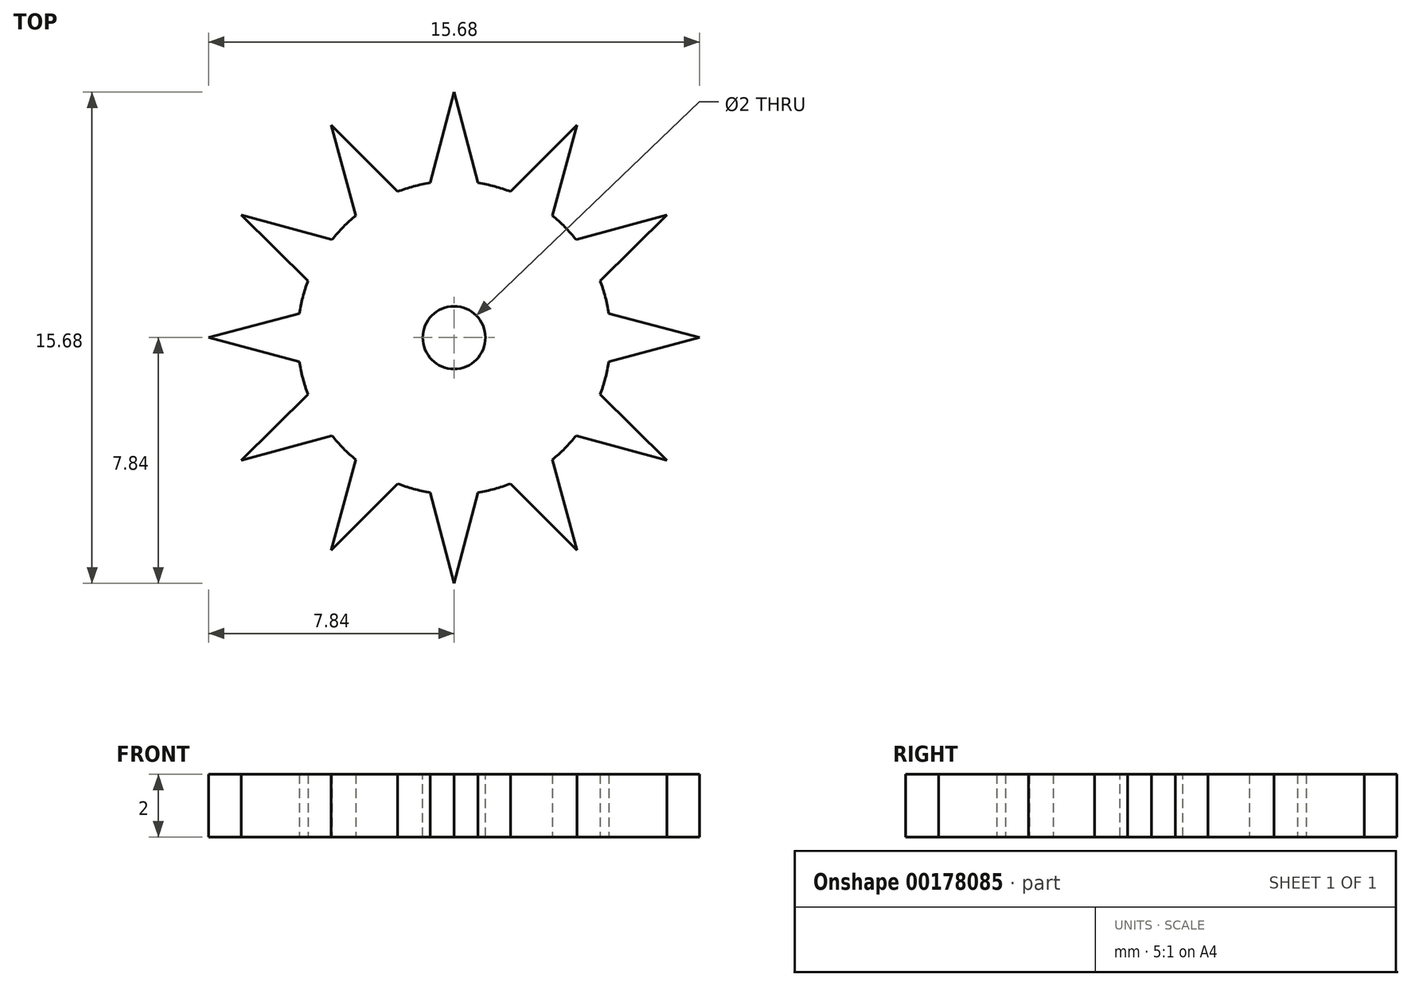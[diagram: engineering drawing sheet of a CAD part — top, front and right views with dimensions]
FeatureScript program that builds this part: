
annotation { "Feature Type Name" : "Feature", "Feature Type Description" : "" }
export const myFeature = defineFeature(function(context is Context, id is Id, definition is map)
    precondition{}
    {
        {
            var Q0;
            Q0=qCreatedBy(makeId("Top.planeOp"),FACE);
            var sketch = newSketch(context, id + "F0", { "sketchPlane" : qUnion([Q0])});
            skCircle(sketch, "E0", {"center": v(0, 0) * mm, "radius": 5 * mm});
            skLineSegment(sketch, "E1", {"start": v(0, 0) * mm, "end": v(0, 5) * mm, "construction": true});
            skLineSegment(sketch, "E2", {"start": v(0, 7.84) * mm, "end": v(-0.77, 4.94) * mm});
            skLineSegment(sketch, "E3.MirrorCS", {"start": v(0, 7.84) * mm, "end": v(0.77, 4.94) * mm});
            skLineSegment(sketch, "E4.1.0", {"start": v(-3.92, 6.8) * mm, "end": v(-1.8, 4.66) * mm});
            skLineSegment(sketch, "E4.1.1", {"start": v(-3.92, 6.8) * mm, "end": v(-3.13, 3.9) * mm});
            skLineSegment(sketch, "E4.2.0", {"start": v(-6.8, 3.92) * mm, "end": v(-3.9, 3.13) * mm});
            skLineSegment(sketch, "E4.2.1", {"start": v(-6.8, 3.92) * mm, "end": v(-4.66, 1.8) * mm});
            skLineSegment(sketch, "E4.3.0", {"start": v(-7.84, 0) * mm, "end": v(-4.94, 0.77) * mm});
            skLineSegment(sketch, "E4.3.1", {"start": v(-7.84, 0) * mm, "end": v(-4.94, -0.77) * mm});
            skLineSegment(sketch, "E4.4.0", {"start": v(-6.8, -3.92) * mm, "end": v(-4.66, -1.8) * mm});
            skLineSegment(sketch, "E4.4.1", {"start": v(-6.8, -3.92) * mm, "end": v(-3.9, -3.13) * mm});
            skLineSegment(sketch, "E4.5.0", {"start": v(-3.92, -6.8) * mm, "end": v(-3.13, -3.9) * mm});
            skLineSegment(sketch, "E4.5.1", {"start": v(-3.92, -6.8) * mm, "end": v(-1.8, -4.66) * mm});
            skLineSegment(sketch, "E4.6.0", {"start": v(0, -7.84) * mm, "end": v(-0.77, -4.94) * mm});
            skLineSegment(sketch, "E4.6.1", {"start": v(0, -7.84) * mm, "end": v(0.77, -4.94) * mm});
            skLineSegment(sketch, "E4.7.0", {"start": v(3.92, -6.8) * mm, "end": v(1.8, -4.66) * mm});
            skLineSegment(sketch, "E4.7.1", {"start": v(3.92, -6.8) * mm, "end": v(3.13, -3.9) * mm});
            skLineSegment(sketch, "E4.8.0", {"start": v(6.8, -3.92) * mm, "end": v(3.9, -3.13) * mm});
            skLineSegment(sketch, "E4.8.1", {"start": v(6.8, -3.92) * mm, "end": v(4.66, -1.8) * mm});
            skLineSegment(sketch, "E4.9.0", {"start": v(7.84, 0) * mm, "end": v(4.94, -0.77) * mm});
            skLineSegment(sketch, "E4.9.1", {"start": v(7.84, 0) * mm, "end": v(4.94, 0.77) * mm});
            skLineSegment(sketch, "E5.2.10.0", {"start": v(6.8, 3.92) * mm, "end": v(4.66, 1.8) * mm});
            skLineSegment(sketch, "E5.3.10.0", {"start": v(6.8, 3.92) * mm, "end": v(3.9, 3.13) * mm});
            skLineSegment(sketch, "E5.2.11.0", {"start": v(3.92, 6.8) * mm, "end": v(3.13, 3.9) * mm});
            skLineSegment(sketch, "E5.3.11.0", {"start": v(3.92, 6.8) * mm, "end": v(1.8, 4.66) * mm});
            skSolve(sketch);
        }
        {
            var Q0;
            Q0=qSketchRegion(id+"F0",true);
            extrude(context, id + "F1", {"entities" : qUnion([Q0]), "depth" : 2 * mm});
        }
        {
            var Q0;
            Q0=makeQuery(id+"F1.opExtrude","CAP_FACE",FACE,{"disambiguationData":[OSD([sQuery(id+"F0.wireOp",EDGE,"E0"),sQuery(id+"F0.wireOp",EDGE,"E2"),sQuery(id+"F0.wireOp",EDGE,"E3.MirrorCS"),sQuery(id+"F0.wireOp",EDGE,"E4.1.0"),sQuery(id+"F0.wireOp",EDGE,"E4.1.1"),sQuery(id+"F0.wireOp",EDGE,"E4.2.0"),sQuery(id+"F0.wireOp",EDGE,"E4.2.1"),sQuery(id+"F0.wireOp",EDGE,"E4.3.0"),sQuery(id+"F0.wireOp",EDGE,"E4.3.1"),sQuery(id+"F0.wireOp",EDGE,"E4.4.0"),sQuery(id+"F0.wireOp",EDGE,"E4.4.1"),sQuery(id+"F0.wireOp",EDGE,"E4.5.0"),sQuery(id+"F0.wireOp",EDGE,"E4.5.1"),sQuery(id+"F0.wireOp",EDGE,"E4.6.0"),sQuery(id+"F0.wireOp",EDGE,"E4.6.1"),sQuery(id+"F0.wireOp",EDGE,"E4.7.0"),sQuery(id+"F0.wireOp",EDGE,"E4.7.1"),sQuery(id+"F0.wireOp",EDGE,"E4.8.0"),sQuery(id+"F0.wireOp",EDGE,"E4.8.1"),sQuery(id+"F0.wireOp",EDGE,"E4.9.0"),sQuery(id+"F0.wireOp",EDGE,"E4.9.1"),sQuery(id+"F0.wireOp",EDGE,"E4.10.0"),sQuery(id+"F0.wireOp",EDGE,"E4.10.1"),sQuery(id+"F0.wireOp",EDGE,"E4.11.0"),sQuery(id+"F0.wireOp",EDGE,"E4.11.1"),sQuery(id+"F0.wireOp",EDGE,"E4.12.0"),sQuery(id+"F0.wireOp",EDGE,"E4.12.1"),sQuery(id+"F0.wireOp",EDGE,"E4.13.0"),sQuery(id+"F0.wireOp",EDGE,"E4.13.1"),sQuery(id+"F0.wireOp",EDGE,"E4.14.0"),sQuery(id+"F0.wireOp",EDGE,"E4.14.1"),sQuery(id+"F0.wireOp",EDGE,"E4.15.0"),sQuery(id+"F0.wireOp",EDGE,"E4.15.1")])],"isStart":false});
            var sketch = newSketch(context, id + "F2", { "sketchPlane" : qUnion([Q0])});
            skCircle(sketch, "E6", {"center": v(0, 0) * mm, "radius": 1 * mm});
            skSolve(sketch);
        }
        {
            var Q0;
            Q0 = qSketchRegion(id + "F2", true);
            extrude(context, id + "F3", {"entities" : qUnion([Q0]), "operationType" : NewBodyOperationType.REMOVE, "oppositeDirection" : true, "depth" : 25 * mm});
        }
    });
